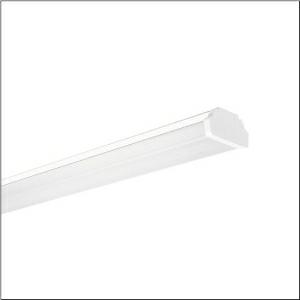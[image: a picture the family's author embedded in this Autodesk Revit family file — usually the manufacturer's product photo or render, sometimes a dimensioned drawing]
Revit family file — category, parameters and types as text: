
# Revit family: dus_r__31_gen_2_53bd812dv6a5c2_b68b
name_source: partatom
category: Lighting Fixtures
units: mm (PartAtom-declared; Revit-internal decimal feet)

## family parameters
Cut with Voids When Loaded = No
Host = Face
Light Source = No
Part Type = Normal
Room Calculation Point = No
Round Connector Dimension = Use Diameter
Shared = No

## types (1)
- --- (1 x LED, 10550 lm, 61.4 W, 6500K)
    Apparent Load = 61 VA
    CIE Flux Codes = 47 80 95 93 100
    Color Rendering = 80
    Color Temperature = 6500K
    Default Elevation = 1800 mm
    Description = DUS® 31 Gen.2, luminaire insert, of sheet steel, coil coated, white, length: 1.535mm, width: 81mm, height: 90mm, 5x system unit, system units: 307mm, LED rated luminous flux: 10.550lm, light colour: 865, control gear: DALI 2, control gear: ECG DALI, with plug, 5-pole, with phase selection, mains connection: 220..240V, AC, 50/60Hz, rated input power: 61W, through-wiring accessed according to module size, primary optical cover: cover, of PMMA, light emission: direct distribution, primary light characteristic: symmetric, protection rating (complete): IP20, protection rating (LED compartment): IP50, insulation class (complete): insulation class I (protective earthing), certification: CE, ENEC, VDE, UKCA, impact resistance: IK03, permissible ambient temperature for indoor applications: -25..+35°C, corresponds to IFS (International Featured Standards) requirements for safety and quality in the food industry, reducing of maximum allowable ambient temperature of 5°C with ceiling mounting, packaging unit: 1 piece
    Height = 95 mm
    Lamp = 1 x LED
    Lamp Light Flux = 10550 lm
    Lamp Power = 61.4 W
    Lamp count = 1
    Length = 1535 mm
    Luminous efficacy = 172 lm/W
    Manufacturer = Siteco
    ModVariant = No
    Model = 53BD812DV6A5C2
    Mounting Place = Ceiling
    Mounting Type = Pendant
    Number of Poles = 1
    OnlyDefault = Yes
    Power Factor = 1
    Product Name = DUS® 31 Gen.2
    Product group = luminaire insert | ceiling pendant
    ProductGroupID = 902
    Protection Class = Protection class I
    Protection Degree = IP 20
    RLX_Detail_Level = 1
    RLX_Emergency_Light_Flux = 0 lm
    RLX_Emergency_Type = 0
    RLX_Emergency_Type_DB = No
    RlxData = <blob elided: 32081 chars, md5=1ba21ebd>
    Socket = socket
    Standby Power = 0 W
    System Light Flux = 10550 lm
    System Power = 61 W
    Type Comments = factory setting: luminous flux: 100 % | dim-lin: 254 | 418 mA
    Type Image = l_1319596.jpg
    URL = http://relux.com
    VarID = @adj_063225
    Voltage = 0 V
    Weight = 0.00 kg
    Width = 81 mm

## geometry (parser evidence)
native form markers: Blend x4, Sweep x13
no freeform markers — native parametric forms only
